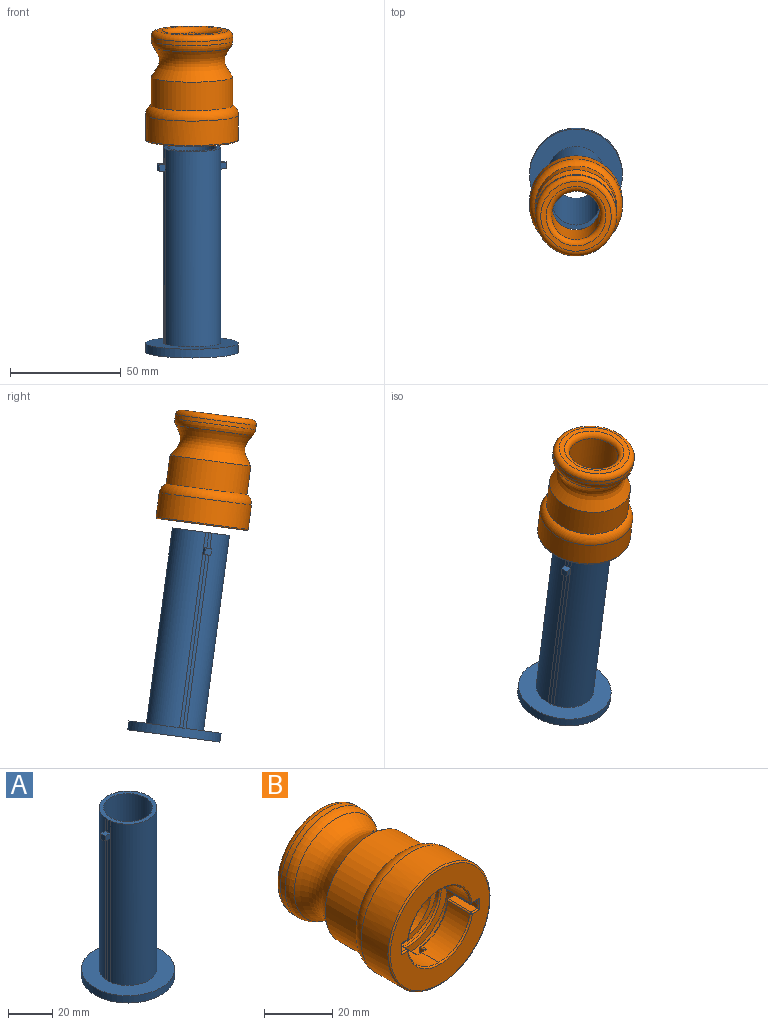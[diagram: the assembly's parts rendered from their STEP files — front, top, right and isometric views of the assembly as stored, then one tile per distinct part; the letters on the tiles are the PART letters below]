
ASSEMBLY  parts=2 mates=1
PART A: 25 faces, bbox 42x42x93 mm
  f0: extruded ~79x1.5mm, area 118.7mm2, adj f1,f4,f9,f24
  f1: extruded ~79x1.5mm, area 118.7mm2, adj f0,f4,f10,f24
  f2: extruded ~79x1.5mm, area 118.7mm2, adj f3,f4,f9,f22
  f3: extruded ~79x1.5mm, area 118.7mm2, adj f2,f4,f10,f22
  f4: plane 42.02x42.02mm, normal (0,0,1), area 854.4mm2, adj f0,f1,f2,f3,f6,f9,f10
  f5: plane 42x42mm, normal (0,0,-1), area 1005.3mm2, adj f6,f13
  f6: cylinder r=21mm len=42mm, axis (0,0,-1), area 527.8mm2, adj f4,f5
  f7: extruded ~7x1.5mm, area 10.5mm2, adj f8,f9,f20,f23
  f8: extruded ~7x1.5mm, area 10.5mm2, adj f7,f10,f20,f23
  f9: cylinder r=13mm len=89mm, axis (0,0,-1), area 3367.2mm2, adj f0,f2,f4,f7,f11,f15,f19,f20
  f10: cylinder r=13mm len=89mm, axis (0,0,-1), area 3367.2mm2, adj f1,f3,f4,f8,f12,f14,f17,f20
  f11: extruded ~7x1.5mm, area 10.5mm2, adj f9,f12,f20,f21
  f12: extruded ~7x1.5mm, area 10.5mm2, adj f10,f11,f20,f21
  f13: cylinder r=11mm len=93mm, axis (0,0,-1), area 6427.7mm2, adj f5,f20
  f14: plane 3.02x3mm, normal (0,1,0), area 9mm2, adj f10,f16,f21,f22
  f15: plane 3.02x3mm, normal (0,-1,0), area 9mm2, adj f9,f16,f21,f22
  f16: extruded ~3x3mm, area 9mm2, adj f14,f15,f21,f22
  f17: plane 3.02x3mm, normal (0,1,0), area 9mm2, adj f10,f18,f23,f24
  f18: extruded ~3x3mm, area 9mm2, adj f17,f19,f23,f24
  f19: plane 3.02x3mm, normal (0,-1,0), area 9mm2, adj f9,f18,f23,f24
  f20: plane 26x26mm, normal (0,0,1), area 150.8mm2, adj f7,f8,f9,f10,f11,f12,f13
  f21: plane 3.09x3mm, normal (0,0,1), area 9mm2, adj f11,f12,f14,f15,f16
  f22: plane 3.09x3mm, normal (0,0,-1), area 9mm2, adj f2,f3,f14,f15,f16
  f23: plane 3.09x3mm, normal (0,0,1), area 9mm2, adj f7,f8,f17,f18,f19
  f24: plane 3.09x3mm, normal (0,0,-1), area 9mm2, adj f0,f1,f17,f18,f19
PART B: 63 faces, bbox 45.5x50x45.5 mm
  f0: plane 41x41mm, normal (0,-1,0), area 724.5mm2, adj f32,f33,f35,f41,f47,f50,f53,f54
  f1: plane 14.54x14.54mm, normal (0,1,0), area 49.9mm2, adj f3,f29,f34,f38
  f2: plane 14.54x14.54mm, normal (0,1,0), area 50mm2, adj f5,f20,f26,f52
  f3: cylinder r=16mm len=17.6mm, axis (0,-1,0), area 85mm2, adj f1,f4,f23,f24,f28,f30,f32,f33
  f4: plane 17.74x17.74mm, normal (0,-1,0), area 66mm2, adj f3,f23,f24,f51
  f5: cylinder r=16mm len=17.6mm, axis (0,-1,0), area 91.4mm2, adj f2,f6,f19,f21,f22,f25,f26,f27
  f6: plane 17.74x17.74mm, normal (0,-1,0), area 66mm2, adj f5,f19,f25,f39
  f7: cylinder r=13mm len=26mm, axis (0,-1,0), area 705.1mm2, adj f8,f9,f36,f38,f39,f40,f41,f42
  f8: cylinder r=13mm len=12.84mm, axis (0,-1,0), area 161.4mm2, adj f7,f46,f49,f52,f56,f60
  f9: plane 26x26mm, normal (0,-1,0), area 150.8mm2, adj f7,f13
  f10: revolved ~36.8x36.8mm, area 1548.4mm2, adj f15,f18
  f11: cylinder r=18.4mm len=36.8mm, axis (0,-1,0), area 215.6mm2, adj f16,f18
  f12: plane 31.8x31.8mm, normal (0,1,0), area 221.7mm2, adj f16,f17
  f13: cylinder r=11mm len=32.9mm, axis (0,-1,0), area 2273.9mm2, adj f9,f17
  f14: cylinder r=21mm len=42mm, axis (0,-1,0), area 1466.4mm2, adj f61,f62
  f15: cylinder r=18.4mm len=36.8mm, axis (0,-1,0), area 1502.9mm2, adj f10,f62
  f16: torus R=15.9mm, axis (0,1,0), area 431.6mm2, adj f11,f12
  f17: torus R=13.5mm, axis (0,1,0), area 293.8mm2, adj f12,f13
  f18: torus R=13.4mm, axis (0,1,0), area 353.9mm2, adj f10,f11
  f19: plane 12.5x2.59mm, normal (0,0,-1), area 32.3mm2, adj f5,f6,f22,f39,f40,f47
  f20: plane 9.5x2.58mm, normal (0,0,1), area 24.5mm2, adj f2,f21,f52,f56,f57
  f21: extruded ~9.5x1.6mm, area 15.2mm2, adj f5,f20,f22,f53
  f22: extruded ~9.5x1.6mm, area 15.2mm2, adj f5,f19,f21,f50
  f23: plane 5.01x2.59mm, normal (-1,0,0), area 12.9mm2, adj f3,f4,f30,f31,f45,f48,f51
  f24: plane 12.5x2.59mm, normal (0,0,1), area 32.3mm2, adj f3,f4,f33,f51,f54,f55
  f25: plane 5.01x2.59mm, normal (1,0,0), area 12.9mm2, adj f5,f6,f27,f39,f43,f46
  f26: plane 2.59x2mm, normal (-1,0,0), area 5.2mm2, adj f2,f5,f27,f46,f49,f52
  f27: plane 3.2x2.6mm, normal (0,1,0), area 8mm2, adj f5,f25,f26,f46
  f28: extruded ~2x1.6mm, area 3.2mm2, adj f3,f29,f30,f31
  f29: plane 2.59x2mm, normal (1,0,0), area 5.2mm2, adj f1,f28,f31,f38,f42,f45
  f30: extruded ~2x1.6mm, area 3.2mm2, adj f3,f23,f28,f31
  f31: plane 3.2x2.6mm, normal (0,1,0), area 8mm2, adj f23,f28,f29,f30,f45
  f32: extruded ~10x2.1mm, area 16.1mm2, adj f0,f3,f33,f34,f35
  f33: extruded ~10x2.1mm, area 16.1mm2, adj f0,f3,f24,f32,f54
  f34: plane 9.5x2.59mm, normal (0,0,-1), area 24.5mm2, adj f1,f32,f35,f36,f38
  f35: cylinder r=0.5mm len=2.58mm, axis (1,0,0), area 2mm2, adj f0,f32,f34,f37
  f36: cylinder r=0.5mm len=9.5mm, axis (0,-1,0), area 6.5mm2, adj f7,f34,f37,f38
  f37: sphere r=0.5mm, area 0.4mm2, adj f35,f36,f41
  f38: torus R=13.5mm, axis (0,-1,0), area 13.5mm2, adj f1,f7,f29,f34,f36,f42
  f39: torus R=13.5mm, axis (0,-1,0), area 19mm2, adj f6,f7,f19,f25,f40,f43
  f40: cylinder r=0.5mm len=13mm, axis (0,-1,0), area 9mm2, adj f7,f19,f39,f44
  f41: torus R=13.5mm, axis (0,-1,0), area 29.3mm2, adj f0,f7,f37,f44
  f42: cylinder r=0.5mm len=2.5mm, axis (0,-1,0), area 1.4mm2, adj f7,f29,f38,f45
  f43: cylinder r=0.5mm len=6mm, axis (0,-1,0), area 3.9mm2, adj f7,f25,f39,f46
  f44: sphere r=0.5mm, area 0.4mm2, adj f40,f41,f47
  f45: torus R=13.5mm, axis (0,-1,0), area 2.7mm2, adj f7,f23,f29,f31,f42,f48
  f46: torus R=13.5mm, axis (0,-1,0), area 2.7mm2, adj f7,f8,f25,f26,f27,f43,f49
  f47: cylinder r=0.5mm len=3.05mm, axis (1,0,0), area 2.2mm2, adj f0,f19,f44,f50
  f48: cylinder r=0.5mm len=6mm, axis (0,-1,0), area 3.9mm2, adj f7,f23,f45,f51
  f49: cylinder r=0.5mm len=2.5mm, axis (0,-1,0), area 1.4mm2, adj f8,f26,f46,f52
  f50: bspline ~3.07x0.66mm, area 1.5mm2, adj f0,f22,f47,f53
  f51: torus R=13.5mm, axis (0,-1,0), area 19mm2, adj f4,f7,f23,f24,f48,f55
  f52: torus R=13.5mm, axis (0,-1,0), area 13.5mm2, adj f2,f8,f20,f26,f49,f56
  f53: bspline ~3.07x0.66mm, area 1.5mm2, adj f0,f21,f50,f57
  f54: cylinder r=0.5mm len=2.58mm, axis (-1,0,0), area 2mm2, adj f0,f24,f33,f58
  f55: cylinder r=0.5mm len=13mm, axis (0,-1,0), area 9mm2, adj f7,f24,f51,f58
  f56: cylinder r=0.5mm len=9.5mm, axis (0,-1,0), area 6.5mm2, adj f8,f20,f52,f59
  f57: cylinder r=0.5mm len=3.05mm, axis (-1,0,0), area 2.2mm2, adj f0,f20,f53,f59
  f58: sphere r=0.5mm, area 0.2mm2, adj f54,f55,f60
  f59: sphere r=0.5mm, area 0.4mm2, adj f56,f57,f60
  f60: torus R=13.5mm, axis (0,-1,0), area 29.3mm2, adj f0,f7,f8,f58,f59
  f61: torus R=20.5mm, axis (0,-1,0), area 102.7mm2, adj f0,f14
  f62: torus R=16mm, axis (0,1,0), area 675.7mm2, adj f14,f15
PLACE A rot(axis=(0.43,-0.06,0.9),17.7deg) t=(12.24,-13.25,79.39)mm
PLACE B rot(axis=(0.98,0.12,0.14),98.6deg) t=(12.24,-25.96,174.88)mm
MATE cylindrical A.f9 <-> B.f11  axis (0,0.13,-0.99) through (12.24,-25.52,171.57)mm
